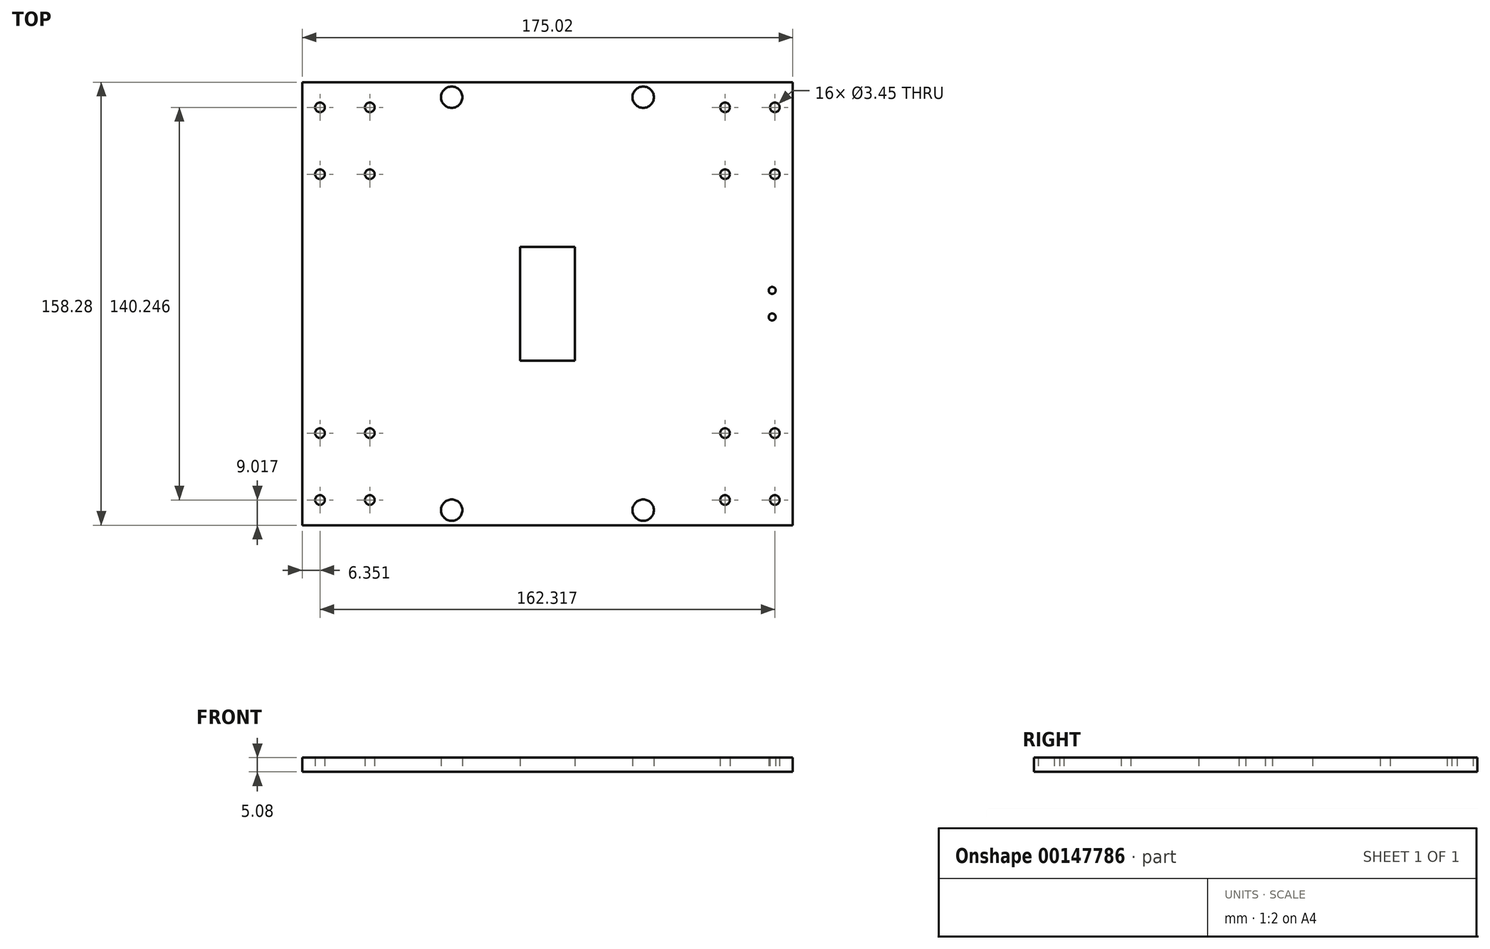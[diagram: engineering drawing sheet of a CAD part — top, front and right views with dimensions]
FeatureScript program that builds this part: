
annotation { "Feature Type Name" : "Feature", "Feature Type Description" : "" }
export const myFeature = defineFeature(function(context is Context, id is Id, definition is map)
    precondition{}
    {
        {
            var Q0;
            Q0=qCreatedBy(makeId("Top.planeOp"),FACE);
            var sketch = newSketch(context, id + "F0", { "sketchPlane" : qUnion([Q0])});
            skLineSegment(sketch, "E0.bottom", {"start": v(87.5, -79.14) * mm, "end": v(-87.5, -79.14) * mm});
            skLineSegment(sketch, "E0.top", {"start": v(87.5, 79.14) * mm, "end": v(-87.5, 79.14) * mm});
            skLineSegment(sketch, "E0.left", {"start": v(87.5, -79.14) * mm, "end": v(87.5, 79.14) * mm});
            skLineSegment(sketch, "E0.right", {"start": v(-87.5, -79.14) * mm, "end": v(-87.5, 79.14) * mm});
            skPoint(sketch, "E0.middle", {"position": v(0, 0) * mm});
            skLineSegment(sketch, "E1", {"start": v(-81.16, 79.14) * mm, "end": v(-81.16, 70.12) * mm, "construction": true});
            skLineSegment(sketch, "E2", {"start": v(-81.16, 70.12) * mm, "end": v(-87.5, 70.12) * mm, "construction": true});
            skLineSegment(sketch, "E3.bottom", {"start": v(-72.27, 58.19) * mm, "end": v(72.27, 58.19) * mm, "construction": true});
            skLineSegment(sketch, "E3.top", {"start": v(-72.27, -58.19) * mm, "end": v(72.27, -58.19) * mm, "construction": true});
            skLineSegment(sketch, "E3.left", {"start": v(-72.27, 58.19) * mm, "end": v(-72.27, -58.19) * mm, "construction": true});
            skLineSegment(sketch, "E3.right", {"start": v(72.27, 58.19) * mm, "end": v(72.27, -58.19) * mm, "construction": true});
            skLineSegment(sketch, "E4.bottom", {"start": v(-81.16, 70.12) * mm, "end": v(-63.38, 70.12) * mm, "construction": true});
            skLineSegment(sketch, "E4.top", {"start": v(-81.16, 46.25) * mm, "end": v(-63.38, 46.25) * mm, "construction": true});
            skLineSegment(sketch, "E4.left", {"start": v(-81.16, 70.12) * mm, "end": v(-81.16, 46.25) * mm, "construction": true});
            skLineSegment(sketch, "E4.right", {"start": v(-63.38, 70.12) * mm, "end": v(-63.38, 46.25) * mm, "construction": true});
            skPoint(sketch, "E4.middle", {"position": v(-72.27, 58.19) * mm});
            skLineSegment(sketch, "E5.bottom", {"start": v(81.16, 70.12) * mm, "end": v(63.38, 70.12) * mm, "construction": true});
            skLineSegment(sketch, "E5.top", {"start": v(81.16, 46.25) * mm, "end": v(63.38, 46.25) * mm, "construction": true});
            skLineSegment(sketch, "E5.left", {"start": v(81.16, 70.12) * mm, "end": v(81.16, 46.25) * mm, "construction": true});
            skLineSegment(sketch, "E5.right", {"start": v(63.38, 70.12) * mm, "end": v(63.38, 46.25) * mm, "construction": true});
            skPoint(sketch, "E5.middle", {"position": v(72.27, 58.19) * mm});
            skLineSegment(sketch, "E6.bottom", {"start": v(81.16, -70.12) * mm, "end": v(63.38, -70.12) * mm, "construction": true});
            skLineSegment(sketch, "E6.top", {"start": v(81.16, -46.25) * mm, "end": v(63.38, -46.25) * mm, "construction": true});
            skLineSegment(sketch, "E6.left", {"start": v(81.16, -70.12) * mm, "end": v(81.16, -46.25) * mm, "construction": true});
            skLineSegment(sketch, "E6.right", {"start": v(63.38, -70.12) * mm, "end": v(63.38, -46.25) * mm, "construction": true});
            skPoint(sketch, "E6.middle", {"position": v(72.27, -58.19) * mm});
            skLineSegment(sketch, "E7.bottom", {"start": v(-63.38, -70.12) * mm, "end": v(-81.16, -70.12) * mm, "construction": true});
            skLineSegment(sketch, "E7.top", {"start": v(-63.38, -46.25) * mm, "end": v(-81.16, -46.25) * mm, "construction": true});
            skLineSegment(sketch, "E7.left", {"start": v(-63.38, -70.12) * mm, "end": v(-63.38, -46.25) * mm, "construction": true});
            skLineSegment(sketch, "E7.right", {"start": v(-81.16, -70.12) * mm, "end": v(-81.16, -46.25) * mm, "construction": true});
            skPoint(sketch, "E7.middle", {"position": v(-72.27, -58.19) * mm});
            skCircle(sketch, "E8", {"center": v(-81.16, 70.12) * mm, "radius": 1.73 * mm});
            skCircle(sketch, "E9", {"center": v(-63.38, 70.12) * mm, "radius": 1.73 * mm});
            skCircle(sketch, "E10", {"center": v(-63.38, 46.25) * mm, "radius": 1.73 * mm});
            skCircle(sketch, "E11", {"center": v(-81.16, 46.25) * mm, "radius": 1.73 * mm});
            skCircle(sketch, "E12", {"center": v(81.16, 46.25) * mm, "radius": 1.73 * mm});
            skCircle(sketch, "E13", {"center": v(81.16, 70.12) * mm, "radius": 1.73 * mm});
            skCircle(sketch, "E14", {"center": v(63.38, 70.12) * mm, "radius": 1.73 * mm});
            skCircle(sketch, "E15", {"center": v(63.38, 46.25) * mm, "radius": 1.73 * mm});
            skCircle(sketch, "E16", {"center": v(81.16, -70.12) * mm, "radius": 1.73 * mm});
            skCircle(sketch, "E17", {"center": v(81.16, -46.25) * mm, "radius": 1.73 * mm});
            skCircle(sketch, "E18", {"center": v(63.38, -46.25) * mm, "radius": 1.73 * mm});
            skCircle(sketch, "E19", {"center": v(63.38, -70.12) * mm, "radius": 1.73 * mm});
            skCircle(sketch, "E20", {"center": v(-63.38, -70.12) * mm, "radius": 1.73 * mm});
            skCircle(sketch, "E21", {"center": v(-63.38, -46.25) * mm, "radius": 1.73 * mm});
            skCircle(sketch, "E22", {"center": v(-81.16, -46.25) * mm, "radius": 1.73 * mm});
            skCircle(sketch, "E23", {"center": v(-81.16, -70.12) * mm, "radius": 1.73 * mm});
            skLineSegment(sketch, "E24.bottom", {"start": v(9.78, 20.32) * mm, "end": v(-9.78, 20.32) * mm});
            skLineSegment(sketch, "E24.top", {"start": v(9.78, -20.32) * mm, "end": v(-9.78, -20.32) * mm});
            skLineSegment(sketch, "E24.left", {"start": v(9.78, 20.32) * mm, "end": v(9.78, -20.32) * mm});
            skLineSegment(sketch, "E24.right", {"start": v(-9.78, 20.32) * mm, "end": v(-9.78, -20.32) * mm});
            skLineSegment(sketch, "E25", {"start": v(87.5, 0) * mm, "end": v(80.2, 0) * mm, "construction": true});
            skLineSegment(sketch, "E26", {"start": v(80.2, 4.75) * mm, "end": v(80.2, -4.75) * mm, "construction": true});
            skCircle(sketch, "E27", {"center": v(80.2, 4.75) * mm, "radius": 1.25 * mm});
            skCircle(sketch, "E28", {"center": v(80.2, -4.75) * mm, "radius": 1.25 * mm});
            skLineSegment(sketch, "E29", {"start": v(-63.38, -70.12) * mm, "end": v(-34.17, -70.12) * mm, "construction": true});
            skLineSegment(sketch, "E30", {"start": v(-34.17, -70.12) * mm, "end": v(-34.17, -73.74) * mm, "construction": true});
            skLineSegment(sketch, "E31", {"start": v(-34.17, -73.74) * mm, "end": v(-34.17, -79.14) * mm, "construction": true});
            skCircle(sketch, "E32", {"center": v(-34.17, -73.74) * mm, "radius": 3.8 * mm});
            skLineSegment(sketch, "E33", {"start": v(63.38, -70.12) * mm, "end": v(34.17, -70.12) * mm, "construction": true});
            skLineSegment(sketch, "E34", {"start": v(34.17, -70.12) * mm, "end": v(34.17, -73.74) * mm, "construction": true});
            skLineSegment(sketch, "E35", {"start": v(-63.38, 70.12) * mm, "end": v(-34.17, 70.12) * mm, "construction": true});
            skLineSegment(sketch, "E36", {"start": v(-34.17, 70.12) * mm, "end": v(-34.17, 73.74) * mm, "construction": true});
            skLineSegment(sketch, "E37", {"start": v(63.38, 70.12) * mm, "end": v(34.17, 70.12) * mm, "construction": true});
            skLineSegment(sketch, "E38", {"start": v(34.17, 70.12) * mm, "end": v(34.17, 73.74) * mm, "construction": true});
            skCircle(sketch, "E39", {"center": v(34.17, -73.74) * mm, "radius": 3.8 * mm});
            skCircle(sketch, "E40", {"center": v(-34.17, 73.74) * mm, "radius": 3.8 * mm});
            skCircle(sketch, "E41", {"center": v(34.17, 73.74) * mm, "radius": 3.8 * mm});
            skSolve(sketch);
        }
        {
            var Q0;
            Q0=qSketchRegion(id+"F0",true);
            extrude(context, id + "F1", {"entities" : qUnion([Q0]), "depth" : 5.08 * mm});
        }
    });
